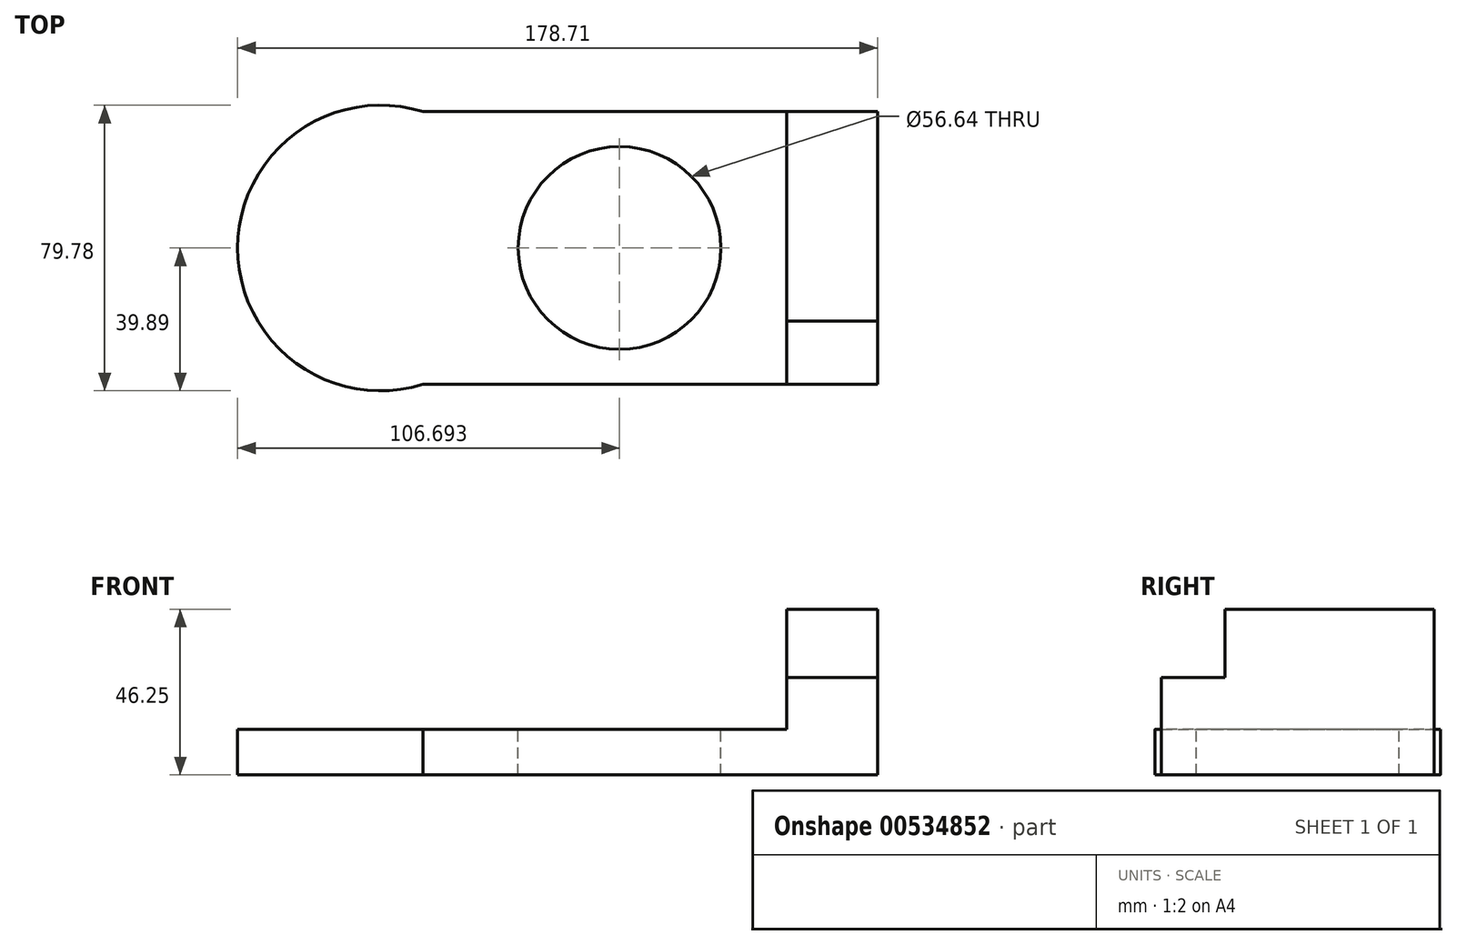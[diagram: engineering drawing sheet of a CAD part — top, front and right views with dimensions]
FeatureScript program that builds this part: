
annotation { "Feature Type Name" : "Feature", "Feature Type Description" : "" }
export const myFeature = defineFeature(function(context is Context, id is Id, definition is map)
    precondition{}
    {
        {
            var Q0;
            Q0=qCreatedBy(makeId("Top.planeOp"),FACE);
            var sketch = newSketch(context, id + "F0", { "sketchPlane" : qUnion([Q0])});
            skLineSegment(sketch, "E0.bottom", {"start": v(63.5, 38.1) * mm, "end": v(-63.5, 38.1) * mm});
            skLineSegment(sketch, "E0.top", {"start": v(63.5, -38.1) * mm, "end": v(-63.5, -38.1) * mm});
            skLineSegment(sketch, "E0.left", {"start": v(63.5, 38.1) * mm, "end": v(63.5, -38.1) * mm});
            skLineSegment(sketch, "E0.right", {"start": v(-63.5, 38.1) * mm, "end": v(-63.5, -38.1) * mm});
            skPoint(sketch, "E0.middle", {"position": v(0, 0) * mm});
            skArc(sketch, "E1", {"start": v(-63.5, 38.1) * mm, "mid": v(-115.2, 0) * mm, "end": v(-63.5, -38.1) * mm});
            skSolve(sketch);
        }
        {
            var Q0;
            Q0 = qSketchRegion(id + "F0", true);
            extrude(context, id + "F1", {"entities" : qUnion([Q0]), "depth" : 12.7 * mm, "offsetDistance" : 25.4 * mm});
        }
        {
            var Q0;
            Q0=qCreatedBy(makeId("Front.planeOp"),FACE);
            var sketch = newSketch(context, id + "F2", { "sketchPlane" : qUnion([Q0])});
            skLineSegment(sketch, "E2.bottom", {"start": v(38.1, 46.25) * mm, "end": v(63.5, 46.25) * mm});
            skLineSegment(sketch, "E2.top", {"start": v(38.1, 12.7) * mm, "end": v(63.5, 12.7) * mm});
            skLineSegment(sketch, "E2.left", {"start": v(38.1, 46.25) * mm, "end": v(38.1, 12.7) * mm});
            skLineSegment(sketch, "E2.right", {"start": v(63.5, 46.25) * mm, "end": v(63.5, 12.7) * mm});
            skSolve(sketch);
        }
        {
            var Q0;
            Q0 = qSketchRegion(id + "F2", true);
            extrude(context, id + "F3", {"entities" : qUnion([Q0]), "operationType" : NewBodyOperationType.ADD, "endBound" : BoundingType.SYMMETRIC, "depth" : 76.2 * mm, "offsetDistance" : 25.4 * mm});
        }
        {
            var Q0;
            Q0=makeQuery(id+"F3.opExtrude","SWEPT_FACE",FACE,{"disambiguationData":[OSD([sQuery(id+"F2.wireOp",EDGE,"E2.left")])]});
            var sketch = newSketch(context, id + "F4", { "sketchPlane" : qUnion([Q0])});
            skLineSegment(sketch, "E3.bottom", {"start": v(20.39, 46.25) * mm, "end": v(38.1, 46.25) * mm});
            skLineSegment(sketch, "E3.top", {"start": v(20.39, 27.1) * mm, "end": v(38.1, 27.1) * mm});
            skLineSegment(sketch, "E3.left", {"start": v(20.39, 46.25) * mm, "end": v(20.39, 27.1) * mm});
            skLineSegment(sketch, "E3.right", {"start": v(38.1, 46.25) * mm, "end": v(38.1, 27.1) * mm});
            skSolve(sketch);
        }
        {
            var Q0;
            Q0 = qSketchRegion(id + "F4", true);
            extrude(context, id + "F5", {"entities" : qUnion([Q0]), "operationType" : NewBodyOperationType.REMOVE, "endBound" : BoundingType.THROUGH_ALL, "oppositeDirection" : true, "depth" : 25.4 * mm, "offsetDistance" : 25.4 * mm});
        }
        {
            var Q0;
            Q0=makeQuery(id+"F1.opExtrude","CAP_FACE",FACE,{"disambiguationData":[OSD([sQuery(id+"F0.wireOp",EDGE,"E0.bottom"),sQuery(id+"F0.wireOp",EDGE,"E0.top"),sQuery(id+"F0.wireOp",EDGE,"E0.left"),sQuery(id+"F0.wireOp",EDGE,"E0.right")])],"isStart":false});
            var sketch = newSketch(context, id + "F6", { "sketchPlane" : qUnion([Q0])});
            skCircle(sketch, "E4", {"center": v(-8.52, 0) * mm, "radius": 28.32 * mm});
            skSolve(sketch);
        }
        {
            var Q0;
            Q0 = qSketchRegion(id + "F6", true);
            extrude(context, id + "F7", {"entities" : qUnion([Q0]), "operationType" : NewBodyOperationType.REMOVE, "endBound" : BoundingType.THROUGH_ALL, "oppositeDirection" : true, "depth" : 25.4 * mm, "offsetDistance" : 25.4 * mm});
        }
    });
